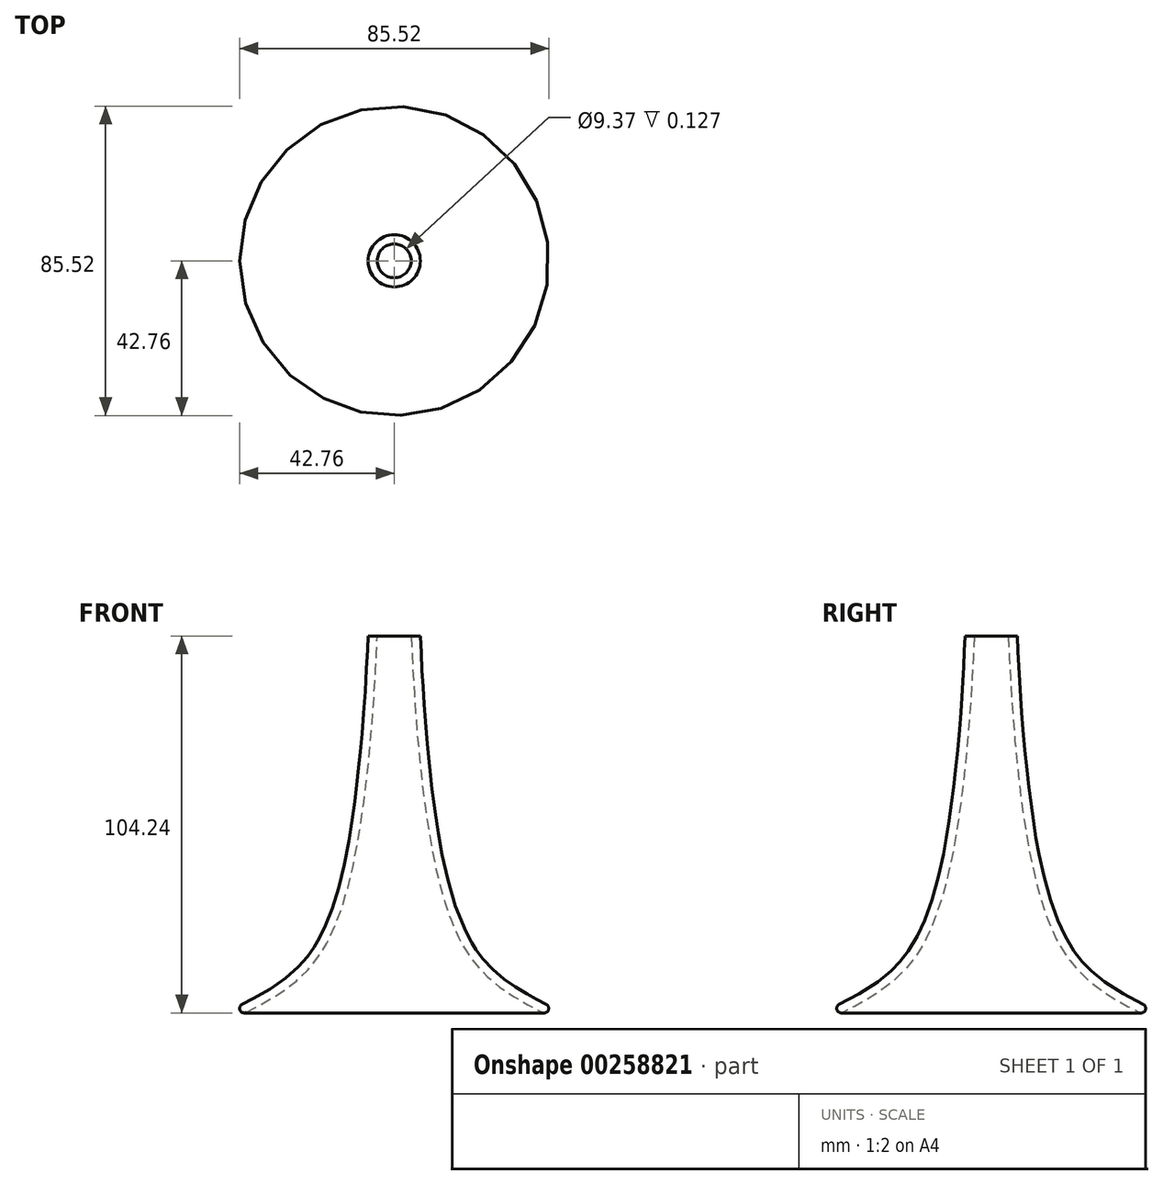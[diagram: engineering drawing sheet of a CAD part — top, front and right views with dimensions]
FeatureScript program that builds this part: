
annotation { "Feature Type Name" : "Feature", "Feature Type Description" : "" }
export const myFeature = defineFeature(function(context is Context, id is Id, definition is map)
    precondition{}
    {
        {
            var Q0;
            Q0=qCreatedBy(makeId("Front.planeOp"),FACE);
            var sketch = newSketch(context, id + "F0", { "sketchPlane" : qUnion([Q0])});
            skFitSpline(sketch, "E0", {"points": [v(40.9, 0) * mm, v(19.98, 16.86) * mm, v(7.5, 65.56) * mm, v(4.68, 103.96) * mm], "startDerivative": vector(-82.71, 44.05) * mm, "endDerivative": vector(-5.32, 106.3) * mm});
            skFitSpline(sketch, "E1.0", {"points": [v(42.1, 2.24) * mm, v(40.37, 3.16) * mm, v(36.96, 4.97) * mm, v(32.13, 7.91) * mm, v(28.44, 10.78) * mm, v(25.73, 13.46) * mm, v(24.14, 15.33) * mm, v(22.94, 16.96) * mm, v(22.08, 18.27) * mm, v(21.25, 19.65) * mm, v(20.19, 21.62) * mm, v(18.94, 24.28) * mm, v(17.11, 28.91) * mm, v(15.15, 35.3) * mm, v(13.25, 43.58) * mm, v(12, 50.73) * mm, v(11.17, 56.44) * mm, v(10.61, 60.67) * mm, v(10.12, 64.82) * mm, v(9.69, 68.84) * mm, v(9.3, 72.73) * mm, v(8.85, 77.76) * mm, v(8.37, 83.79) * mm, v(7.92, 90.72) * mm, v(7.55, 97.45) * mm, v(7.33, 101.87) * mm, v(7.22, 104.09) * mm]});
            skArc(sketch, "E2", {"start": v(42.1, 2.24) * mm, "mid": v(42.61, 0.52) * mm, "end": v(40.9, 0) * mm});
            skLineSegment(sketch, "E3", {"start": v(7.22, 104.09) * mm, "end": v(4.68, 104.09) * mm});
            skLineSegment(sketch, "E4", {"start": v(4.68, 104.09) * mm, "end": v(4.68, 103.96) * mm});
            skLineSegment(sketch, "E5", {"start": v(0, 0) * mm, "end": v(0, 105.5) * mm, "construction": true});
            skSolve(sketch);
        }
        {
            var Q0;
            Q0=makeQuery(id+"F0.imprint","IMPRINT",FACE,{"disambiguationData":[TD([[makeQuery(id+"F0.imprint","IMPRINT",EDGE,{"derivedFrom":sQuery(id+"F0.wireOp",EDGE,"E0")}),-1.0]])]});
            var Q1;
            Q1=sQuery(id+"F0.wireOp",EDGE,"E5");
            revolve(context, id + "F1", {"entities" : qUnion([Q0]), "axis" : qUnion([Q1]), "revolveType" : RevolveType.FULL});
        }
    });
